# Revit family: Vega_D-IP41-syst-BE-en
name_source: partatom
category: Electrical Equipment
units: mm (PartAtom-declared; Revit-internal decimal feet)

## family parameters
Cut with Voids When Loaded = No
Host = Face
Panel Configuration = Two Columns, Circuits Across
Part Type = Panelboard
Room Calculation Point = No
Round Connector Dimension = Use Diameter
Shared = No

## types (14) — shared parameters
EF000003 - Mounting method = EV000384 - Surface mounted (plaster)
EF000007 - Colour = EV000202 - White
EF000008 - Width = 550 mm
EF000049 - Depth = 193 mm  [stored 0.633202 ft]
EF000116 - RAL-number = 9010
EF000339 - Type of cover = EV004216 - Door
EF001062 - EMC-version = No
EF001088 - Extension possible = No
EF001131 - Internal depth = 193 mm  [stored 0.633202 ft]
EF001134 - DIN-rail = No
EF001596 - Material housing = EV000154 - Other
EF002950 - Width in number of modular spacings = 24
EF005474 - Degree of protection (IP) = EV006416 - IP41
EF006306 - With lock = No
EF015776 - Earthing terminal block = No
EF015777 - Neutral terminal block = No
EF015941 - Signal passing door = No
HG000001 - Number of columns = 1
HG000002 - With door or cover = Yes
HG000003 - Range = Vega D
HG000005 - Thickness = 3 mm  [stored 0.00984252 ft]
HG000006 - Flush mounted = No
HG000009 - Double swing door = No
HG000010 - Asymmetric doors = No
Manufacturer = Hager
Type Comments = Vega D
zero-valued in all types: Default Elevation, EF000218 - Built-in depth, EF000332 - Built-in height, EF000846 - Built-in width, HG000007 - Number of empty columns

## per-type parameters (varying)
| type | EF000040 - Height | EF000118 - With mounting plate | EF000266 - Number of rows | EF004462 - Type of closure | EF006244 - Transparent cover/door | EF009212 - Cover model | HG000004 - Manufacturer reference | HG000008 - Number of empty rows | HG000011 - Empty rows from bottom | Model |
| Surface mounted IP41 W550 H1050 D193 24 Modular spacings - FD62BN | 1050 mm | No | 6 | EV000154 - Other | No | EV000116 - Closed | FD62BN | 0 | No | FD62BN |
| Surface mounted IP41 W550 H1050 D193 24 Modular spacings - FD62CN | 1050 mm | No | 6 | EV000154 - Other | Yes | EV009916 - With notch | FD62CN | 0 | No | FD62CN |
| Surface mounted IP41 W550 H1200 D193 24 Modular spacings - FD72BN | 1200 mm | No | 7 | EV000154 - Other | No | EV000116 - Closed | FD72BN | 0 | No | FD72BN |
| Surface mounted IP41 W550 H1200 D193 24 Modular spacings - FD72CN | 1200 mm | No | 7 | EV000154 - Other | Yes | EV009916 - With notch | FD72CN | 0 | No | FD72CN |
| Surface mounted IP41 W550 H450 D193 24 Modular spacings - FD22BN | 450 mm  [stored 1.47638 ft] | No | 2 | 0 | No | EV000116 - Closed | FD22BN | 0 | No | FD22BN |
| Surface mounted IP41 W550 H450 D193 24 Modular spacings - FD22CN | 450 mm  [stored 1.47638 ft] | No | 2 | 0 | Yes | EV009916 - With notch | FD22CN | 0 | No | FD22CN |
| Surface mounted IP41 W550 H600 D193 24 Modular spacings - FD32BN | 600 mm | No | 3 | EV000154 - Other | No | EV000116 - Closed | FD32BN | 0 | No | FD32BN |
| Surface mounted IP41 W550 H600 D193 24 Modular spacings - FD32CN | 600 mm | No | 3 | EV000154 - Other | Yes | EV000116 - Closed | FD32CN | 0 | No | FD32CN |
| Surface mounted IP41 W550 H750 D193 24 Modular spacings - FD42BMN | 750 mm | Yes | 1 | EV000154 - Other | No | EV000116 - Closed | FD42BMN | 3 | Yes | FD42BMN |
| Surface mounted IP41 W550 H750 D193 24 Modular spacings - FD42BN | 750 mm | No | 4 | EV000154 - Other | No | EV000116 - Closed | FD42BN | 0 | No | FD42BN |
| Surface mounted IP41 W550 H750 D193 24 Modular spacings - FD42CN | 750 mm | No | 4 | EV000154 - Other | Yes | EV009916 - With notch | FD42CN | 0 | No | FD42CN |
| Surface mounted IP41 W550 H900 D193 24 Modular spacings - FD52BMN | 900 mm  [stored 2.95276 ft] | Yes | 2 | EV000154 - Other | No | EV000116 - Closed | FD52BMN | 3 | Yes | FD52BMN |
| Surface mounted IP41 W550 H900 D193 24 Modular spacings - FD52BN | 900 mm  [stored 2.95276 ft] | No | 5 | EV000154 - Other | No | EV000116 - Closed | FD52BN | 0 | No | FD52BN |
| Surface mounted IP41 W550 H900 D193 24 Modular spacings - FD52CN | 900 mm  [stored 2.95276 ft] | No | 5 | EV000154 - Other | Yes | EV009916 - With notch | FD52CN | 0 | No | FD52CN |

note: [stored X ft] marks values corroborated as IEEE doubles in the binary element streams (Revit-internal decimal feet)

## geometry (parser evidence)
native form markers: Sweep x11
no freeform markers — native parametric forms only
